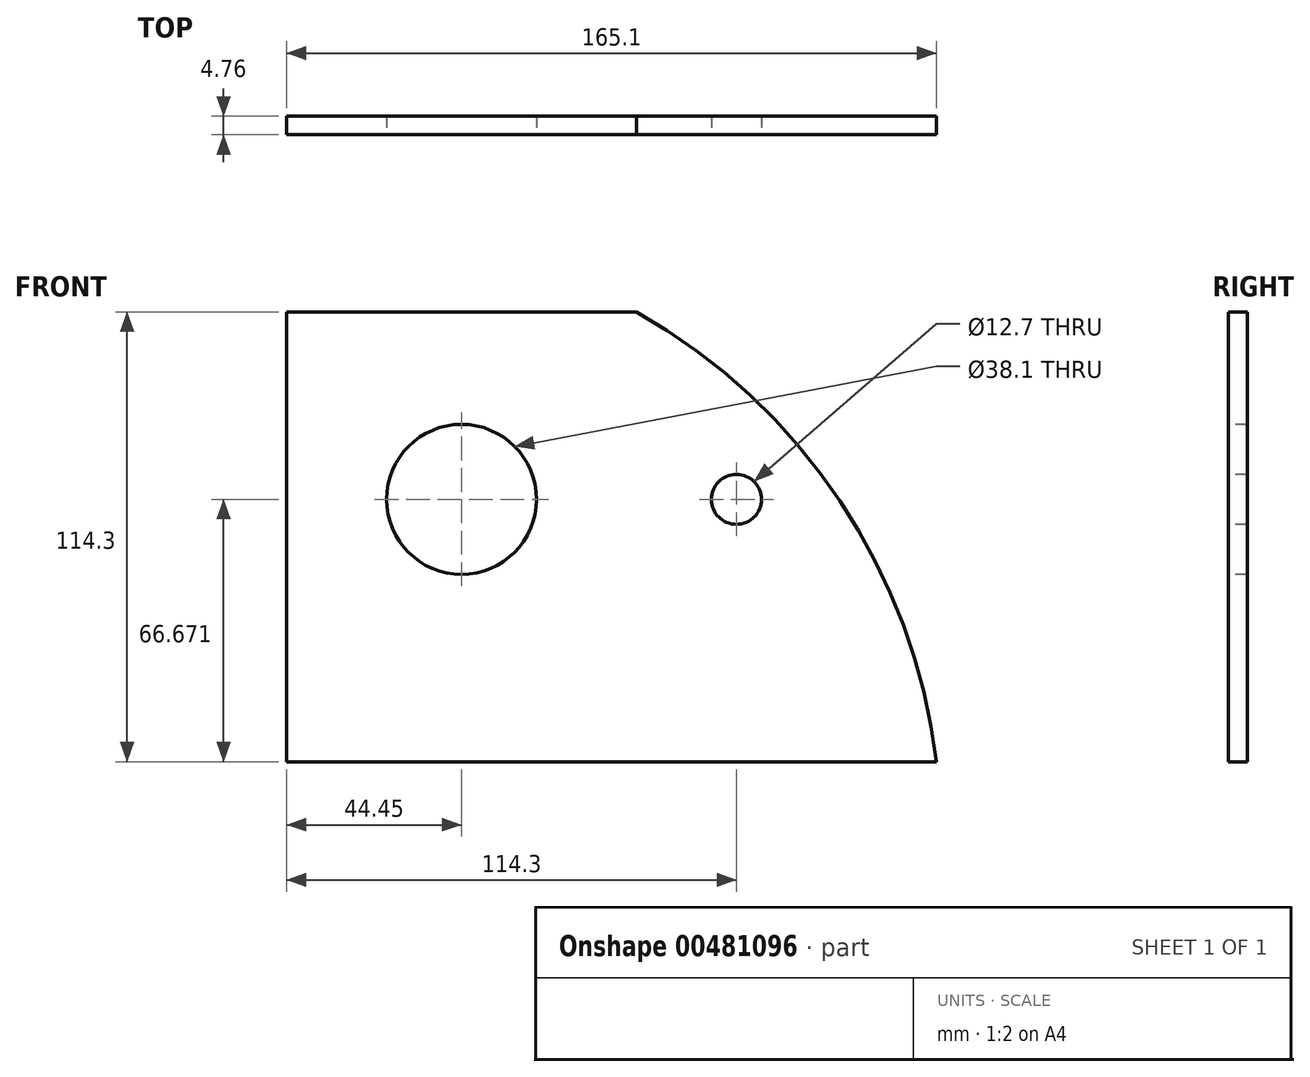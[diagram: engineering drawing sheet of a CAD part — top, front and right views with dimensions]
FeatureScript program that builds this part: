
annotation { "Feature Type Name" : "Feature", "Feature Type Description" : "" }
export const myFeature = defineFeature(function(context is Context, id is Id, definition is map)
    precondition{}
    {
        {
            var Q0;
            Q0=qCreatedBy(makeId("Front.planeOp"),FACE);
            var sketch = newSketch(context, id + "F0", { "sketchPlane" : qUnion([Q0])});
            skLineSegment(sketch, "E0.bottom", {"start": v(0, -3.05) * mm, "end": v(165.1, -3.05) * mm});
            skLineSegment(sketch, "E0.top", {"start": v(0, 111.25) * mm, "end": v(88.9, 111.25) * mm});
            skLineSegment(sketch, "E0.left", {"start": v(0, -3.05) * mm, "end": v(0, 111.25) * mm});
            skLineSegment(sketch, "E1", {"start": v(88.9, -3.05) * mm, "end": v(88.9, 111.25) * mm, "construction": true});
            skArc(sketch, "E2", {"start": v(165.1, -3.05) * mm, "mid": v(140.6, 63.17) * mm, "end": v(88.9, 111.25) * mm});
            skSolve(sketch);
        }
        {
            var Q0;
            Q0 = qSketchRegion(id + "F0", true);
            extrude(context, id + "F1", {"entities" : qUnion([Q0]), "depth" : 4.76 * mm});
        }
        {
            var Q0;
            Q0=makeQuery(id+"F1.opExtrude","CAP_FACE",FACE,{"disambiguationData":[OSD([sQuery(id+"F0.wireOp",EDGE,"E0.bottom"),sQuery(id+"F0.wireOp",EDGE,"E0.top"),sQuery(id+"F0.wireOp",EDGE,"E0.left"),sQuery(id+"F0.wireOp",EDGE,"E2")])],"isStart":false});
            var sketch = newSketch(context, id + "F2", { "sketchPlane" : qUnion([Q0])});
            skLineSegment(sketch, "E3", {"start": v(44.45, 111.25) * mm, "end": v(44.45, -3.05) * mm, "construction": true});
            skCircle(sketch, "E4", {"center": v(44.45, 63.62) * mm, "radius": 19.05 * mm});
            skLineSegment(sketch, "E5", {"start": v(44.45, 63.62) * mm, "end": v(184.15, 63.62) * mm, "construction": true});
            skCircle(sketch, "E6", {"center": v(114.3, 63.62) * mm, "radius": 6.35 * mm});
            skSolve(sketch);
        }
        {
            var Q0;
            Q0 = qSketchRegion(id + "F2", true);
            extrude(context, id + "F3", {"entities" : qUnion([Q0]), "operationType" : NewBodyOperationType.REMOVE, "endBound" : BoundingType.THROUGH_ALL, "oppositeDirection" : true, "depth" : 25.4 * mm});
        }
    });
